# Revit family: efad59ca-4a50-4160-ad04-2817419f50eb
name_source: partatom
category: Generic Models
revit_build: Autodesk Revit 2014 (Build: 20130308_1515(x64)
units: mm (PartAtom-declared; Revit-internal decimal feet)

## types (2) — shared parameters
Assembly Code = D2010700
Depth = 0' - 4"
Height = 1' - 10 1/2"
Installation-Fabrication = http://noblecompany.com
Keynote = 10 28 00
Manufacturer = Noble Company
Manufacturer Fax = 231-799-8850
Manufacturer Website = www.noblecompany.com
Niche Material = Acrylic Polymer Finish
Product Data = http://www.arcat.com
Product Properties = http://noblecompany.com
Revision = R1_09-2016
Sales Information = http://noblecompany.com
URL = www.noblecompany.com

## per-type parameters (varying)
| type | Description | Model | Width |
| 304 Wide Combo | 304 Wide Combo Niche | 304 | 1' - 2 1/4" |
| 305 Narrow Combo | 305 Narrow Combo Niche | 305 | 0' - 8 1/4" |

## geometry (parser evidence)
native form markers: Sweep x1
no freeform markers — native parametric forms only
